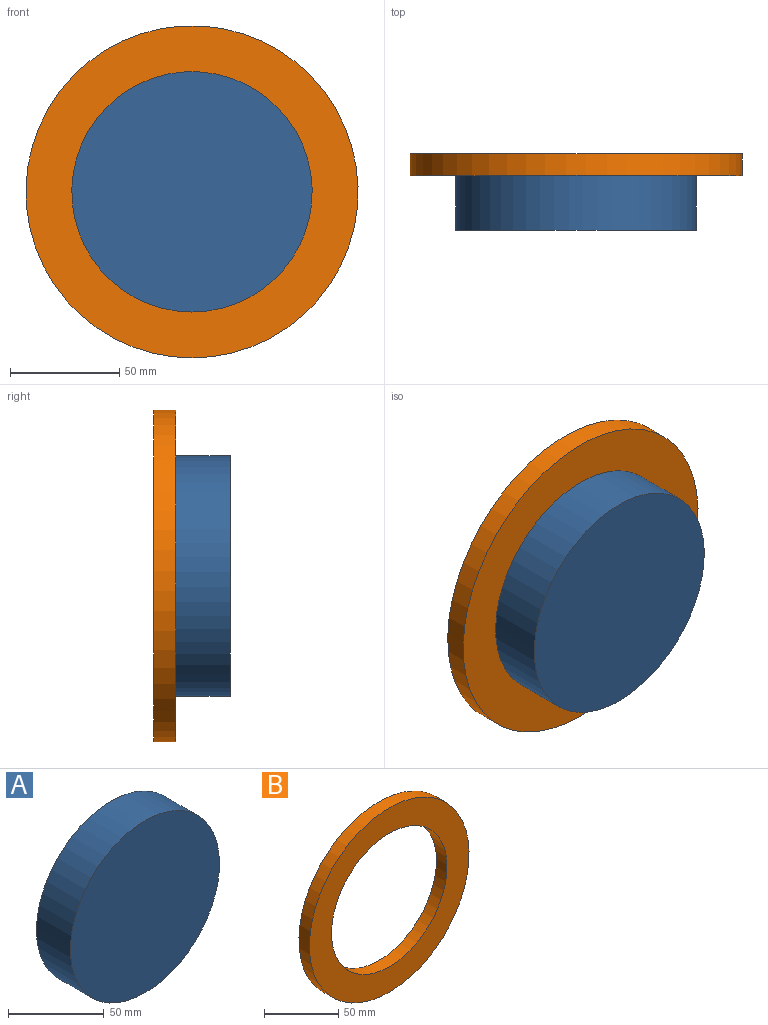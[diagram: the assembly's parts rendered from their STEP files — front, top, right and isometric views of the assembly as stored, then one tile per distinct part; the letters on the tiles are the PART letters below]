
ASSEMBLY  parts=2 mates=1
PART A: 5 faces, bbox 110x25x110 mm
  f0: cylinder r=55mm len=110mm, axis (0,1,0), area 8639.4mm2, adj f1,f2
  f1: plane 110x110mm, normal (0,-1,0), area 9503.3mm2, adj f0
  f2: plane 110x110mm, normal (0,1,0), area 678.6mm2, adj f0,f3
  f3: cylinder r=53mm len=106mm, axis (0,1,0), area 7659.2mm2, adj f2,f4
  f4: plane 106x106mm, normal (0,1,0), area 8824.7mm2, adj f3
PART B: 4 faces, bbox 152x10x152 mm
  f0: cylinder r=55mm len=110mm, axis (0,1,0), area 3455.8mm2, adj f2,f3
  f1: cylinder r=76mm len=152mm, axis (0,1,0), area 4775.2mm2, adj f2,f3
  f2: plane 152x152mm, normal (0,-1,0), area 8642.5mm2, adj f0,f1
  f3: plane 152x152mm, normal (0,1,0), area 8642.5mm2, adj f0,f1
PLACE A t=(-33.47,-33.93,-14.45)mm
PLACE B t=(-33.47,-23.93,-14.45)mm
MATE fastened B.f0 <-> A.f0  axis (0,-1,0) through (-33.47,-33.93,-14.45)mm
